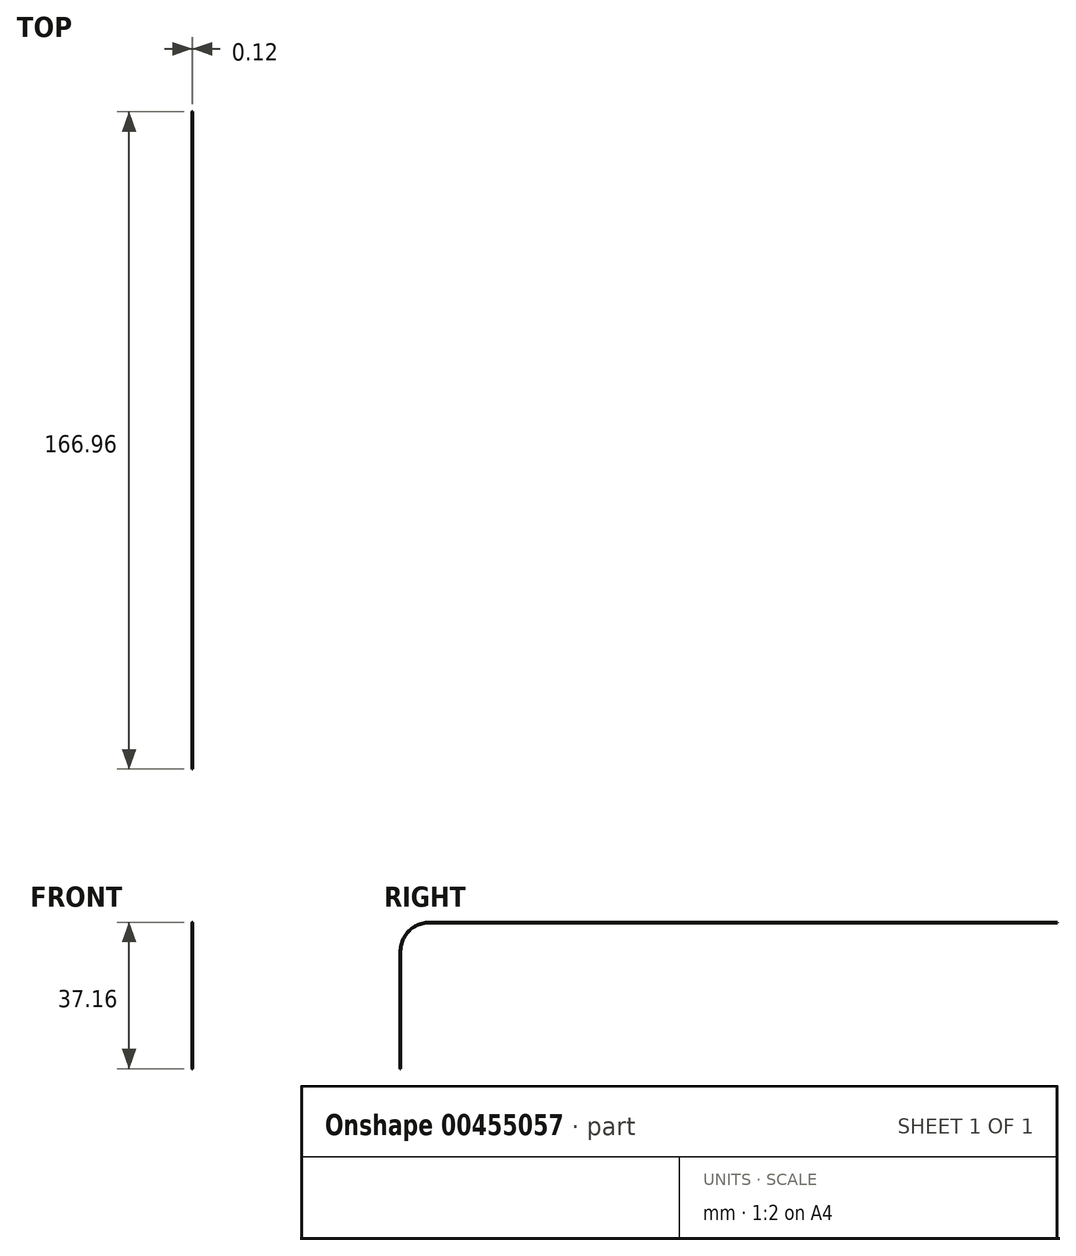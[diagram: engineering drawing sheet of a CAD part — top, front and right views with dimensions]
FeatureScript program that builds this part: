
annotation { "Feature Type Name" : "Feature", "Feature Type Description" : "" }
export const myFeature = defineFeature(function(context is Context, id is Id, definition is map)
    precondition{}
    {
        {
            var Q0;
            Q0=qCreatedBy(makeId("Right.planeOp"),FACE);
            var sketch = newSketch(context, id + "F0", { "sketchPlane" : qUnion([Q0])});
            skLineSegment(sketch, "E0", {"start": v(0, 0) * mm, "end": v(-160, 0) * mm});
            skArc(sketch, "E1", {"start": v(-160, 0) * mm, "mid": v(-164.83, -2.2) * mm, "end": v(-166.9, -7.1) * mm});
            skLineSegment(sketch, "E2", {"start": v(-166.9, -7.1) * mm, "end": v(-166.9, -37.1) * mm});
            skSolve(sketch);
        }
        {
            var Q0;
            Q0=qCreatedBy(makeId("Front.planeOp"),FACE);
            var sketch = newSketch(context, id + "F1", { "sketchPlane" : qUnion([Q0])});
            skCircle(sketch, "E3", {"center": v(0, 0) * mm, "radius": 0.06 * mm});
            skSolve(sketch);
        }
        {
            var Q0;
            Q0 = qSketchRegion(id + "F1", true);
            var Q1;
            Q1 = qConstructionFilter(qBodyType(qCreatedBy(id + "F0" ,EDGE), BodyType.WIRE), ConstructionObject.NO);
            sweep(context, id + "F2", {"profiles" : qUnion([Q0]), "path" : qUnion([Q1])});
        }
    });
